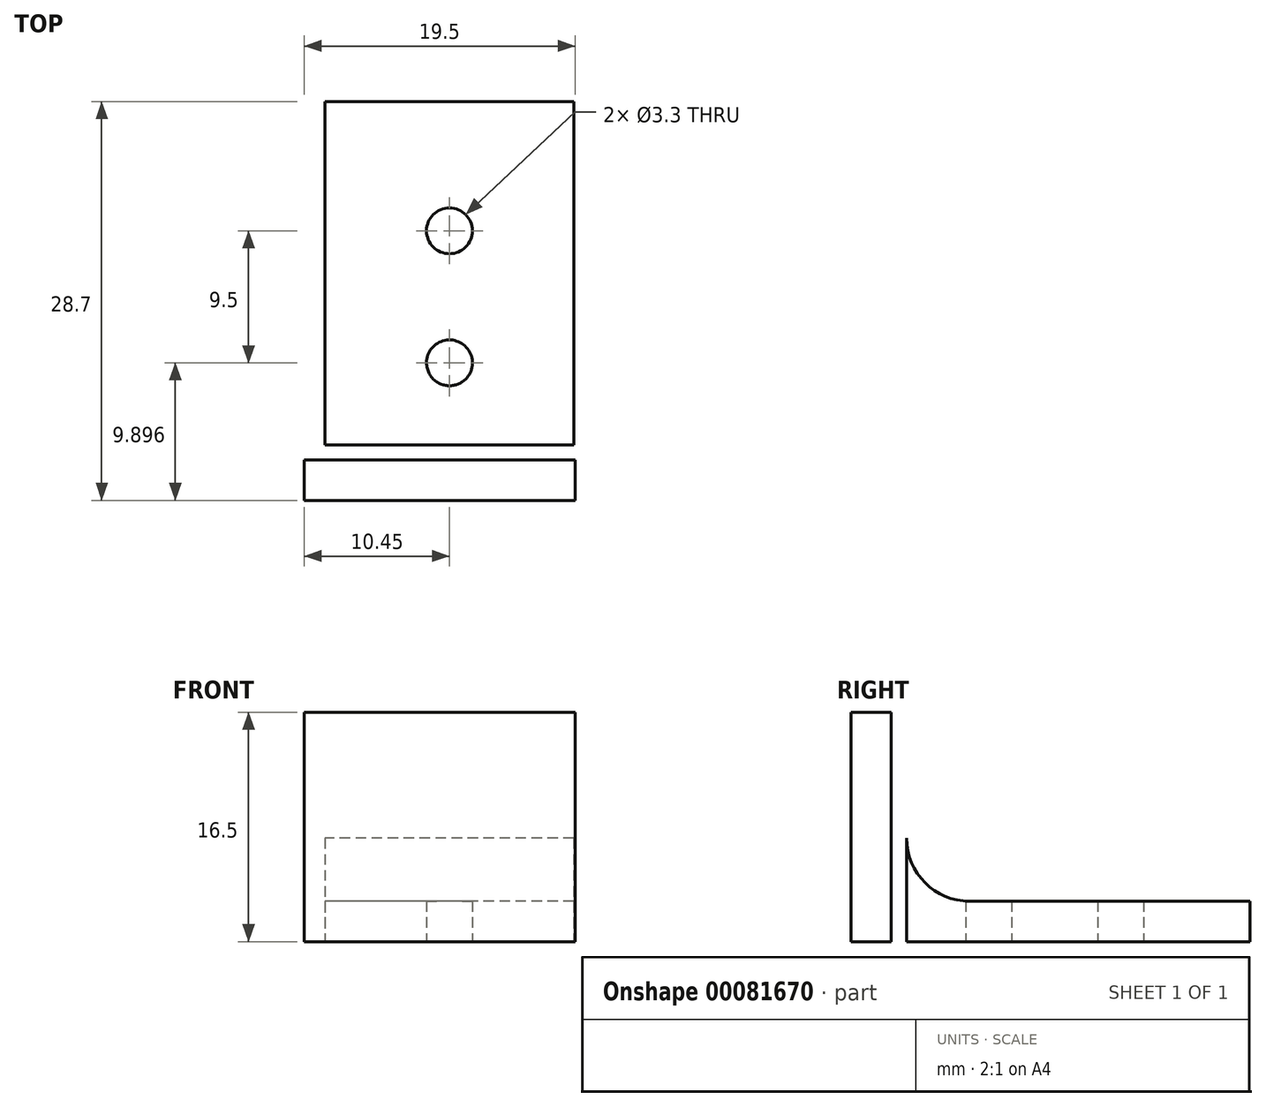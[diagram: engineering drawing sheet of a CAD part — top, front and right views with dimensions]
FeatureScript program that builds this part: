
annotation { "Feature Type Name" : "Feature", "Feature Type Description" : "" }
export const myFeature = defineFeature(function(context is Context, id is Id, definition is map)
    precondition{}
    {
        {
            var Q0;
            Q0=qCreatedBy(makeId("Right.planeOp"),FACE);
            var sketch = newSketch(context, id + "F0", { "sketchPlane" : qUnion([Q0])});
            skLineSegment(sketch, "E0.bottom", {"start": v(-0.58, 16.5) * mm, "end": v(3.42, 16.5) * mm});
            skLineSegment(sketch, "E0.top", {"start": v(-0.58, 0) * mm, "end": v(3.42, 0) * mm});
            skLineSegment(sketch, "E0.left", {"start": v(-0.58, 16.5) * mm, "end": v(-0.58, 0) * mm});
            skLineSegment(sketch, "E0.right", {"start": v(3.42, 16.5) * mm, "end": v(3.42, 7.44) * mm});
            skLineSegment(sketch, "E1.bottom", {"start": v(3.42, 0) * mm, "end": v(9.42, 0) * mm});
            skLineSegment(sketch, "E1.top", {"start": v(7.95, 2.9) * mm, "end": v(9.42, 2.9) * mm});
            skLineSegment(sketch, "E2.bottom", {"start": v(9.42, 2.9) * mm, "end": v(12.52, 2.9) * mm});
            skLineSegment(sketch, "E2.top", {"start": v(9.42, 0) * mm, "end": v(12.52, 0) * mm});
            skLineSegment(sketch, "E3.bottom", {"start": v(12.52, 2.9) * mm, "end": v(22.02, 2.9) * mm});
            skLineSegment(sketch, "E3.top", {"start": v(12.52, 0) * mm, "end": v(22.02, 0) * mm});
            skLineSegment(sketch, "E4.bottom", {"start": v(22.02, 2.9) * mm, "end": v(25.12, 2.9) * mm});
            skLineSegment(sketch, "E4.top", {"start": v(22.02, 0) * mm, "end": v(25.12, 0) * mm});
            skLineSegment(sketch, "E5.bottom", {"start": v(25.12, 2.9) * mm, "end": v(28.12, 2.9) * mm});
            skLineSegment(sketch, "E5.top", {"start": v(25.12, 0) * mm, "end": v(28.12, 0) * mm});
            skLineSegment(sketch, "E5.right", {"start": v(28.12, 2.9) * mm, "end": v(28.12, 0) * mm});
            skLineSegment(sketch, "E6.bottom", {"start": v(-0.58, 16.5) * mm, "end": v(2.32, 16.5) * mm});
            skLineSegment(sketch, "E6.left", {"start": v(-0.58, 16.5) * mm, "end": v(-0.58, 18.1) * mm});
            skLineSegment(sketch, "E6.right", {"start": v(2.32, 16.5) * mm, "end": v(2.32, 18.1) * mm});
            skLineSegment(sketch, "E7", {"start": v(2.32, 18.1) * mm, "end": v(3.42, 18.1) * mm});
            skLineSegment(sketch, "E8", {"start": v(-0.58, 18.1) * mm, "end": v(-0.58, 38.1) * mm});
            skLineSegment(sketch, "E9", {"start": v(-0.58, 38.1) * mm, "end": v(1.42, 38.1) * mm});
            skLineSegment(sketch, "E10", {"start": v(1.42, 38.1) * mm, "end": v(3.42, 18.1) * mm});
            skLineSegment(sketch, "E11", {"start": v(2.32, 16.5) * mm, "end": v(2.32, 0) * mm});
            skPoint(sketch, "E12.newPointA", {"position": v(3.42, 0.1) * mm});
            skArc(sketch, "E12.filletArc", {"start": v(3.42, 7.44) * mm, "mid": v(4.75, 4.23) * mm, "end": v(7.95, 2.9) * mm});
            skLineSegment(sketch, "E13.bottom", {"start": v(2.32, 0) * mm, "end": v(-0.58, 0) * mm});
            skLineSegment(sketch, "E13.top", {"start": v(2.32, -1.5) * mm, "end": v(-0.58, -1.5) * mm});
            skLineSegment(sketch, "E13.left", {"start": v(2.32, 0) * mm, "end": v(2.32, -1.5) * mm});
            skLineSegment(sketch, "E13.right", {"start": v(-0.58, 0) * mm, "end": v(-0.58, -1.5) * mm});
            skLineSegment(sketch, "E14", {"start": v(3.42, 7.44) * mm, "end": v(3.42, 0) * mm});
            skSolve(sketch);
        }
        {
            var Q0;
            {var subQ3=sQuery(id+"F0.wireOp",EDGE,"E0.bottom");Q0=makeQuery(id+"F0.imprint","IMPRINT",FACE,{"disambiguationData":[TD([[makeQuery(id+"F0.imprint","IMPRINT",EDGE,{"derivedFrom":subQ3}),-1.0]])]});}
            var Q1;
            {var subQ3=sQuery(id+"F0.wireOp",EDGE,"gVPVNPHU-9NDZ-KwvJ-QXXo-ELdV5q2nLFK0");Q1=makeQuery(id+"F0.imprint","IMPRINT",FACE,{"disambiguationData":[TD([[makeQuery(id+"F0.imprint","IMPRINT",EDGE,{"derivedFrom":subQ3}),-1.0]])]});}
            var Q2;
            Q2=makeQuery(id+"F0.imprint","IMPRINT",FACE,{"disambiguationData":[TD([[makeQuery(id+"F0.imprint","IMPRINT",EDGE,{"derivedFrom":sQuery(id+"F0.wireOp",EDGE,"E1.bottom")}),1.0]])]});
            var Q3;
            Q3=makeQuery(id+"F0.imprint","IMPRINT",FACE,{"disambiguationData":[TD([[makeQuery(id+"F0.imprint","IMPRINT",EDGE,{"derivedFrom":sQuery(id+"F0.wireOp",EDGE,"E2.bottom")}),-1.0]])]});
            var Q4;
            Q4=makeQuery(id+"F0.imprint","IMPRINT",FACE,{"disambiguationData":[TD([[makeQuery(id+"F0.imprint","IMPRINT",EDGE,{"derivedFrom":sQuery(id+"F0.wireOp",EDGE,"E3.bottom")}),-1.0]])]});
            var Q5;
            Q5=makeQuery(id+"F0.imprint","IMPRINT",FACE,{"disambiguationData":[TD([[makeQuery(id+"F0.imprint","IMPRINT",EDGE,{"derivedFrom":sQuery(id+"F0.wireOp",EDGE,"E4.bottom")}),-1.0]])]});
            var Q6;
            Q6=makeQuery(id+"F0.imprint","IMPRINT",FACE,{"disambiguationData":[TD([[makeQuery(id+"F0.imprint","IMPRINT",EDGE,{"derivedFrom":sQuery(id+"F0.wireOp",EDGE,"E5.bottom")}),-1.0]])]});
            extrude(context, id + "F1", {"entities" : qUnion([Q0, Q1, Q2, Q3, Q4, Q5, Q6]), "depth" : 17.9 * mm});
        }
        {
            var Q0;
            {var subQ0=sQuery(id+"F0.wireOp",EDGE,"E0.left");Q0=makeQuery(id+"F0.imprint","IMPRINT",FACE,{"disambiguationData":[TD([[makeQuery(id+"F0.imprint","IMPRINT",EDGE,{"derivedFrom":subQ0}),1.0]])]});}
            var Q1;
            Q1=makeQuery(id+"F0.imprint","IMPRINT",FACE,{"disambiguationData":[TD([[makeQuery(id+"F0.imprint","IMPRINT",EDGE,{"derivedFrom":sQuery(id+"F0.wireOp",EDGE,"E6.bottom")}),1.0]])]});
            var Q2;
            Q2=makeQuery(id+"F0.imprint","IMPRINT",FACE,{"disambiguationData":[TD([[makeQuery(id+"F0.imprint","IMPRINT",EDGE,{"derivedFrom":sQuery(id+"F0.wireOp",EDGE,"E6.top")}),1.0]])]});
            var Q3;
            Q3=makeQuery(id+"F0.imprint","IMPRINT",FACE,{"disambiguationData":[TD([[makeQuery(id+"F0.imprint","IMPRINT",EDGE,{"derivedFrom":sQuery(id+"F0.wireOp",EDGE,"E13.bottom")}),1.0]])]});
            extrude(context, id + "F2", {"entities" : qUnion([Q0, Q1, Q2, Q3]), "operationType" : NewBodyOperationType.ADD, "depth" : 18 * mm, "hasSecondDirection" : true, "secondDirectionOppositeDirection" : true, "secondDirectionDepth" : 1.5 * mm});
        }
        {
            var Q0;
            Q0=makeQuery(id+"F1.opExtrude","SWEPT_FACE",FACE,{"disambiguationData":[OSD([sQuery(id+"F0.wireOp",EDGE,"E0.top"),sQuery(id+"F0.wireOp",EDGE,"E1.bottom"),sQuery(id+"F0.wireOp",EDGE,"E2.top"),sQuery(id+"F0.wireOp",EDGE,"E3.top"),sQuery(id+"F0.wireOp",EDGE,"E4.top"),sQuery(id+"F0.wireOp",EDGE,"E5.top")])]});
            var sketch = newSketch(context, id + "F3", { "sketchPlane" : qUnion([Q0])});
            skLineSegment(sketch, "E15.bottom", {"start": v(0, -2.32) * mm, "end": v(17.9, -2.32) * mm});
            skLineSegment(sketch, "E15.top", {"start": v(0, -9.32) * mm, "end": v(17.9, -9.32) * mm});
            skLineSegment(sketch, "E15.left", {"start": v(0, -2.32) * mm, "end": v(0, -9.32) * mm});
            skLineSegment(sketch, "E15.right", {"start": v(17.9, -2.32) * mm, "end": v(17.9, -9.32) * mm});
            skLineSegment(sketch, "E16.top", {"start": v(0, -18.82) * mm, "end": v(17.9, -18.82) * mm});
            skLineSegment(sketch, "E16.left", {"start": v(0, -9.32) * mm, "end": v(0, -18.82) * mm});
            skLineSegment(sketch, "E16.right", {"start": v(17.9, -9.32) * mm, "end": v(17.9, -18.82) * mm});
            skLineSegment(sketch, "E17", {"start": v(8.95, -9.32) * mm, "end": v(8.95, -18.82) * mm});
            skSolve(sketch);
        }
        {
            var Q0;
            Q0=sQuery(id+"F3.wireOp",VERTEX,"E17.start");
            var Q1;
            Q1=sQuery(id+"F3.wireOp",VERTEX,"E17.end");
            var Q2;
            Q2=makeQuery(id+"F1.opExtrude","SWEPT_BODY",BODY,{"disambiguationData":[OSD([sQuery(id+"F0.wireOp",EDGE,"E0.bottom"),sQuery(id+"F0.wireOp",EDGE,"E0.top"),sQuery(id+"F0.wireOp",EDGE,"E0.right"),sQuery(id+"F0.wireOp",EDGE,"E1.bottom"),sQuery(id+"F0.wireOp",EDGE,"E1.top"),sQuery(id+"F0.wireOp",EDGE,"E2.bottom"),sQuery(id+"F0.wireOp",EDGE,"E2.top"),sQuery(id+"F0.wireOp",EDGE,"E3.bottom"),sQuery(id+"F0.wireOp",EDGE,"E3.top"),sQuery(id+"F0.wireOp",EDGE,"E4.bottom"),sQuery(id+"F0.wireOp",EDGE,"E4.top"),sQuery(id+"F0.wireOp",EDGE,"E5.bottom"),sQuery(id+"F0.wireOp",EDGE,"E5.top"),sQuery(id+"F0.wireOp",EDGE,"E5.right"),sQuery(id+"F0.wireOp",EDGE,"E11"),sQuery(id+"F0.wireOp",EDGE,"E12.filletArc")])]});
            hole(context, id + "F4", {"style" : HoleStyle.SIMPLE, "endStyle" : HoleEndStyle.THROUGH, "standardTappedOrClearance" : lookupTablePath({ "standard" : "ISO", "fit" : "Normal", "size" : "M3", "type" : "Clearance" }), "standardBlindInLast" : lookupTablePath({ "fit" : "Standard", "standard" : "ISO", "size" : "M3", "type" : "Clearance" }), "holeDiameter" : 3.3 * mm, "locations" : qUnion([Q0, Q1]), "scope" : qUnion([Q2]), "isTappedThrough" : true});
        }
    });
